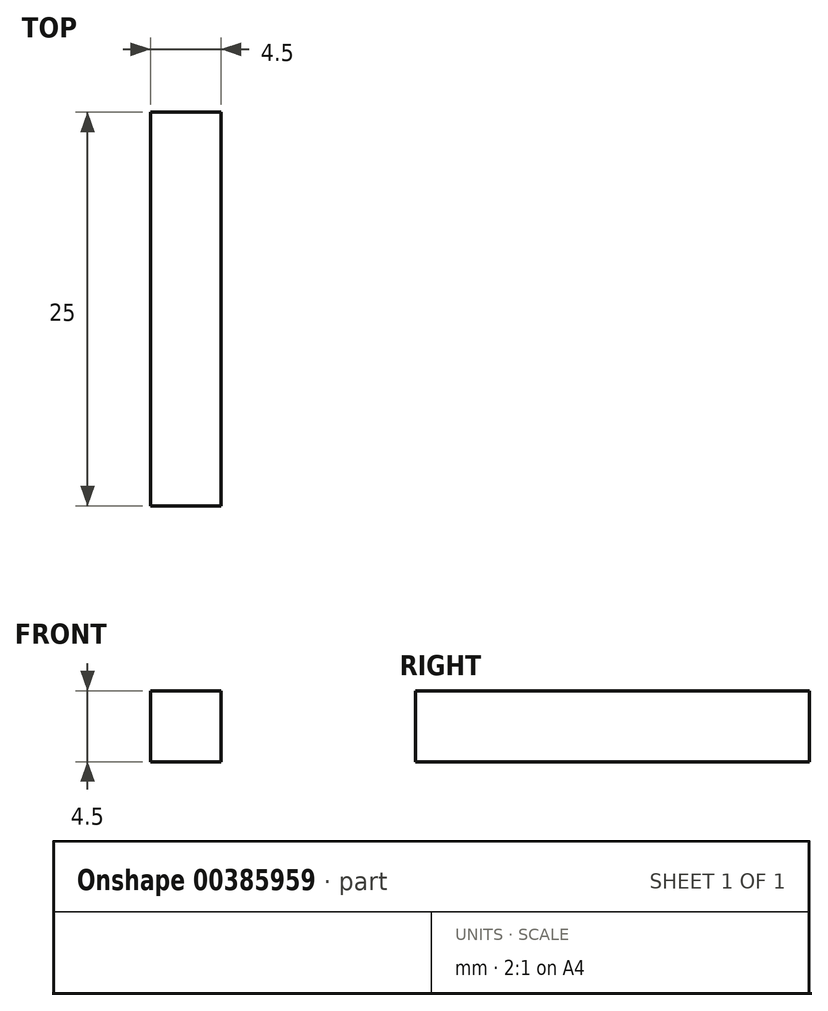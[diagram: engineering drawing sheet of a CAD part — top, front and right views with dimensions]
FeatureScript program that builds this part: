
annotation { "Feature Type Name" : "Feature", "Feature Type Description" : "" }
export const myFeature = defineFeature(function(context is Context, id is Id, definition is map)
    precondition{}
    {
        {
            var Q0;
            Q0=qCreatedBy(makeId("Front.planeOp"),FACE);
            var sketch = newSketch(context, id + "F0", { "sketchPlane" : qUnion([Q0])});
            skLineSegment(sketch, "E0.bottom", {"start": v(-2.25, 2.25) * mm, "end": v(2.25, 2.25) * mm});
            skLineSegment(sketch, "E0.top", {"start": v(-2.25, -2.25) * mm, "end": v(2.25, -2.25) * mm});
            skLineSegment(sketch, "E0.left", {"start": v(-2.25, 2.25) * mm, "end": v(-2.25, -2.25) * mm});
            skLineSegment(sketch, "E0.right", {"start": v(2.25, 2.25) * mm, "end": v(2.25, -2.25) * mm});
            skSolve(sketch);
        }
        {
            var Q0;
            Q0 = qSketchRegion(id + "F0", true);
            extrude(context, id + "F1", {"entities" : qUnion([Q0]), "depth" : 25 * mm});
        }
    });
